# Revit family: HD062-2016.04.29-BT-ScreenPanel_J
name_source: partatom
category: Generic Models
revit_build: Autodesk Revit 2016 (Build: 20150714_1515(x64)
units: mm (PartAtom-declared; Revit-internal decimal feet)

## family parameters
Always vertical = Yes
Can host rebar = No
Cut with Voids When Loaded = No
Part Type = Normal
Room Calculation Point = No
Round Connector Dimension = Use Diameter
Shared = No
Work Plane-Based = No

## types (1)
- Productos HD
    BT_Alto = 481 modulo maximo
    BT_Ancho = 50 mm (espesor)
    BT_Codigo_Origen = HD062
    BT_Color = 100 colores
    BT_Descripcion = Screenpanel J
    BT_EETT = El panel deberá tener una geometría rectangular y plana, formado por

un fleje tipo piel, plegado en todo su perímetro, con un espesor total 

de 50mm,

El panel es fabricado en aluzinc con un espesor de 1 ó 1,2mm

El avance útil del panel es de 484mm.

El esquema de pintura considera la aplicación de un primer poliéster 

de secado al horno por ambas caras, con un espesor de 5 ± 2 micras, 

y la aplicación de un esmalte de terminación poliéster secado al horno 

por ambas caras, con un espesor total de 25 ± 2 micras (incluido el 

primer).

La instalación del panel deberá ser Horizontal y considera el uso de 

un perfil guia tipo J de dimensiones 50 x 18mm en espesor 1,5mm y 

material aluzinc

Opciones de perforado estándar: #110M1 - #110M3 - #111 - #114 -

#115 - #116 - #401 - #402 - #403 - #150 - #151 - #405 - #406 -

#407 - #408 - #420
    BT_Elemento = Paneles y Revestimientos verticales
    BT_Especialidad = Arquitectura
    BT_Fabricante = Hunter Douglas
    BT_Itemizado_Estandar_CDT = D 01 08 04
    BT_Linea = A pedido
    BT_Marca = Hunter Douglas
    BT_MasterFormat® = 07 42 13
    BT_Material = AZ-AL-ACC
    BT_Nombre_Comercial = ScreenPanel J
    BT_Nombre_Corto = ScreenPanel J
    BT_Nombre_Tecnico = ScreenPanel J
    BT_Profundidad = 3500 mm (alto)
    BT_SKU = 003627
    BT_Uso = Exterior / Interior
    BT_Web_del_Producto = http://www.hunterdouglas.cl
    ID_Objeto = BT_F_F_335
    ID_Source = BIMTOOL
    Material = Metal
    URL = http://www.hunterdouglas.cl

## geometry (parser evidence)
native form markers: Sweep x32
no freeform markers — native parametric forms only
